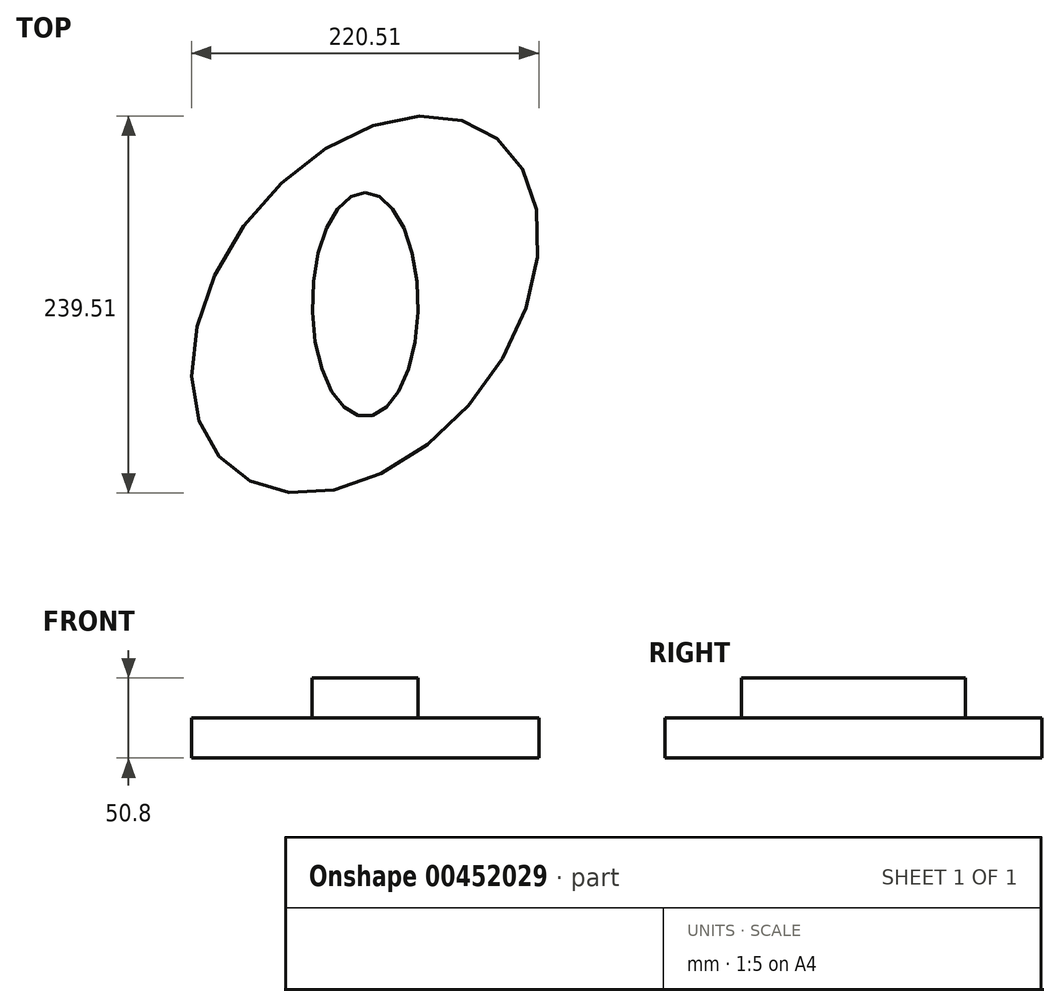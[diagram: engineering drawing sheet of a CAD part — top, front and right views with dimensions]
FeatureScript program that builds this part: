
annotation { "Feature Type Name" : "Feature", "Feature Type Description" : "" }
export const myFeature = defineFeature(function(context is Context, id is Id, definition is map)
    precondition{}
    {
        {
            var Q0;
            Q0=qCreatedBy(makeId("Top.planeOp"),FACE);
            var sketch = newSketch(context, id + "F0", { "sketchPlane" : qUnion([Q0])});
            skEllipse(sketch, "E0", {"center": v(-57.3, -50.5) * mm, "majorRadius": 134.58 * mm, "minorRadius": 91.57 * mm, "majorAxis": v(0.62, 0.78)});
            skSolve(sketch);
        }
        {
            var Q0;
            Q0 = qSketchRegion(id + "F0", true);
            extrude(context, id + "F1", {"entities" : qUnion([Q0]), "depth" : 25.4 * mm, "offsetDistance" : 25.4 * mm});
        }
        {
            var Q0;
            Q0=makeQuery(id+"F1.opExtrude","CAP_FACE",FACE,{"disambiguationData":[OSD([sQuery(id+"F0.wireOp",EDGE,"E0")])],"isStart":false});
            var sketch = newSketch(context, id + "F2", { "sketchPlane" : qUnion([Q0])});
            skEllipse(sketch, "E1", {"center": v(-57.3, -50.5) * mm, "majorRadius": 71.08 * mm, "minorRadius": 33.65 * mm, "majorAxis": v(0, 1)});
            skSolve(sketch);
        }
        {
            var Q0;
            Q0 = qSketchRegion(id + "F2", true);
            extrude(context, id + "F3", {"entities" : qUnion([Q0]), "depth" : 25.4 * mm, "offsetDistance" : 25.4 * mm});
        }
    });
